# Revit family: Reihenschutzgerät
name_source: partatom
category: Generic Models
revit_build: Autodesk Revit 2015 (Build: 20140606_1530(x64)
units: mm (PartAtom-declared; Revit-internal decimal feet)

## types (14) — shared parameters
Height = 99 mm
Length = 9 mm  [stored 0.0295276 ft]
Manufacturer = OBO Bettermann
Material = OBO PA GF20
URL = http://www.obo-bettermann.com
Width = 100 mm  [stored 0.328084 ft]

## per-type parameters (varying)
| type | GTIN | Manufacturer Art.No. |
| MDP-2 D-5-T | 4012195406839 | 5098404 |
| MDP-3 D-5-T | 4012195406846 | 5098407 |
| MDP-4 D-5-T | 4012195406853 | 5098411 |
| MDP-2 D-24-T | 4012195406860 | 5098422 |
| MDP-3 D-24-T | 4012195406877 | 5098427 |
| MDP-4 D-24-T | 4012195406884 | 5098431 |
| MDP-2 D-48-T | 4012195406891 | 5098442 |
| MDP-3 D-48-T | 4012195406907 | 5098446 |
| MDP-4 D-48-T | 4012195406914 | 5098450 |
| MDP-4 D-5-T-10 | 4012195625124 | 5098413 |
| MDP-2 D-12-T-10 | 4012195787372 | 5098415 |
| MDP-4 D-12-T-10 | 4012195773610 | 5098419 |
| MDP-2 D-24-T-10 | 4012195787389 | 5098425 |
| MDP-4 D-24-T-10 | 4012195625131 | 5098433 |

note: column(s) folded — value = type name in every type: Article Type

note: [stored X ft] marks values corroborated as IEEE doubles in the binary element streams (Revit-internal decimal feet)

## geometry (parser evidence)
native form markers: Sweep x2
no freeform markers — native parametric forms only
